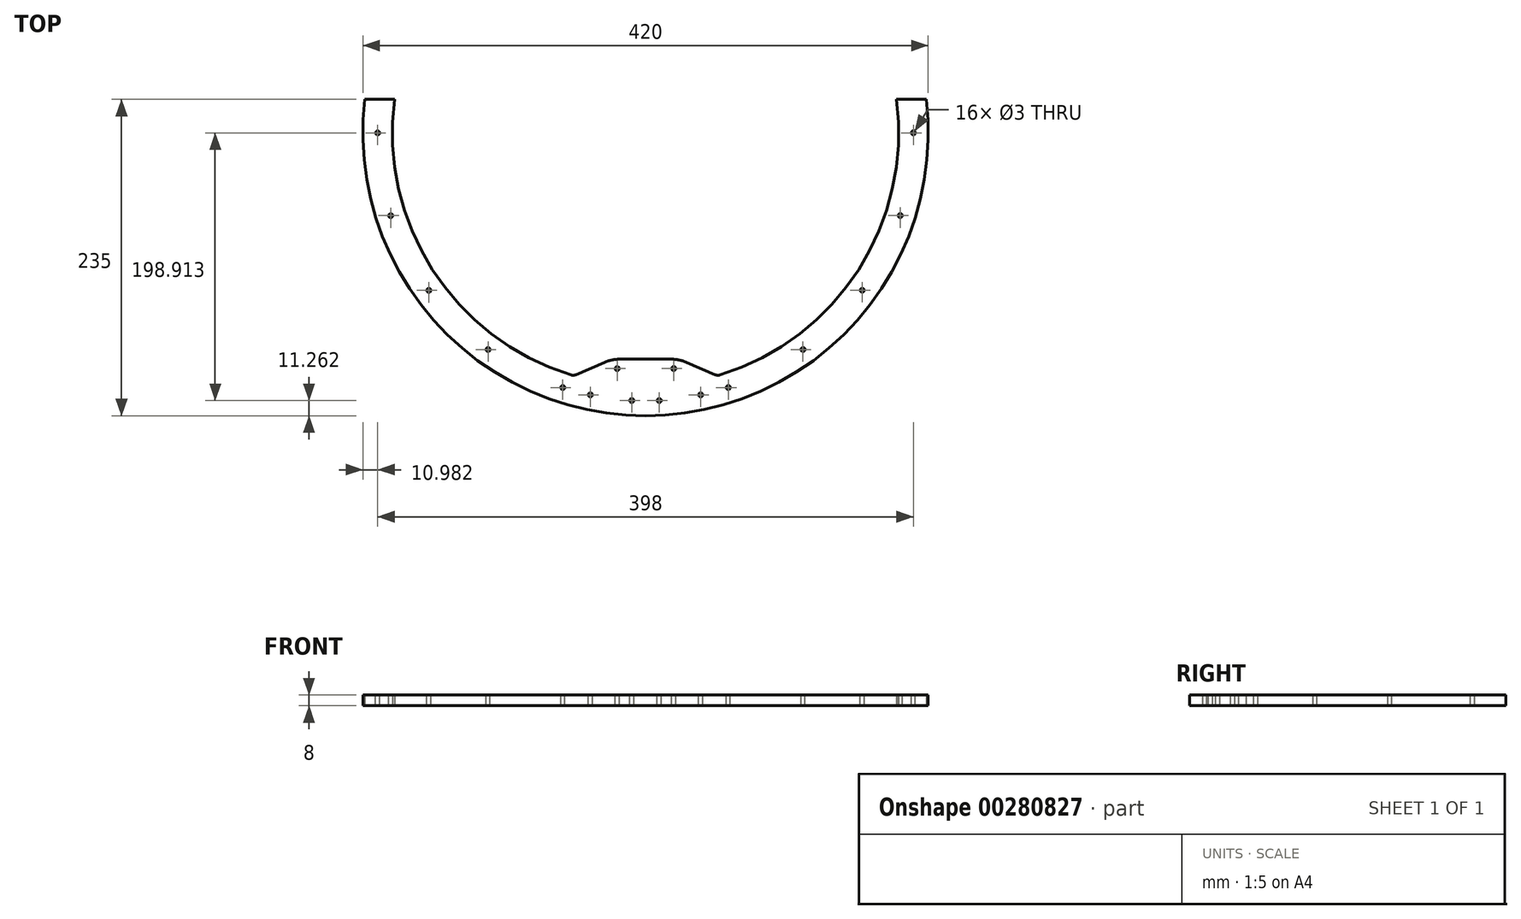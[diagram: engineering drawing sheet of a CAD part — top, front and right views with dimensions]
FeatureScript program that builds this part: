
annotation { "Feature Type Name" : "Feature", "Feature Type Description" : "" }
export const myFeature = defineFeature(function(context is Context, id is Id, definition is map)
    precondition{}
    {
        {
            var Q0;
            Q0=qCreatedBy(makeId("Top.planeOp"),FACE);
            var sketch = newSketch(context, id + "F0", { "sketchPlane" : qUnion([Q0])});
            skArc(sketch, "E0", {"start": v(-186.33, 25) * mm, "mid": v(-157.8, -102.18) * mm, "end": v(-53.43, -180.25) * mm});
            skArc(sketch, "E1", {"start": v(-208.5, 25) * mm, "mid": v(0, -210) * mm, "end": v(208.5, 25) * mm});
            skLineSegment(sketch, "E2", {"start": v(0, 0) * mm, "end": v(-114.72, 0) * mm, "construction": true});
            skLineSegment(sketch, "E3", {"start": v(0, 0) * mm, "end": v(0, 25) * mm, "construction": true});
            skLineSegment(sketch, "E4", {"start": v(186.33, 25) * mm, "end": v(208.5, 25) * mm});
            skLineSegment(sketch, "E5.MirrorCS", {"start": v(-186.33, 25) * mm, "end": v(-208.5, 25) * mm});
            skLineSegment(sketch, "E6", {"start": v(0, -188) * mm, "end": v(0, -168) * mm, "construction": true});
            skLineSegment(sketch, "E7", {"start": v(0, -168) * mm, "end": v(25, -168) * mm});
            skLineSegment(sketch, "E8", {"start": v(25, -168) * mm, "end": v(53.43, -180.25) * mm});
            skLineSegment(sketch, "E9.MirrorCS", {"start": v(0, -168) * mm, "end": v(-25, -168) * mm});
            skLineSegment(sketch, "E10.MirrorCS", {"start": v(-25, -168) * mm, "end": v(-53.43, -180.25) * mm});
            skArc(sketch, "E11.trimOffspring", {"start": v(53.43, -180.25) * mm, "mid": v(157.8, -102.18) * mm, "end": v(186.33, 25) * mm});
            skPoint(sketch, "E12.orphan", {"position": v(0, 25) * mm});
            skSolve(sketch);
        }
        {
            var Q0;
            Q0=qSketchRegion(id+"F0",true);
            extrude(context, id + "F1", {"entities" : qUnion([Q0]), "depth" : 8 * mm});
        }
        {
            var Q0;
            Q0=makeQuery(id+"F1.opExtrude","CAP_FACE",FACE,{"disambiguationData":[OSD([sQuery(id+"F0.wireOp",EDGE,"E0"),sQuery(id+"F0.wireOp",EDGE,"E1"),sQuery(id+"F0.wireOp",EDGE,"E4"),sQuery(id+"F0.wireOp",EDGE,"E5.MirrorCS"),sQuery(id+"F0.wireOp",EDGE,"E7"),sQuery(id+"F0.wireOp",EDGE,"E8"),sQuery(id+"F0.wireOp",EDGE,"E9.MirrorCS"),sQuery(id+"F0.wireOp",EDGE,"E10.MirrorCS"),sQuery(id+"F0.wireOp",EDGE,"E11.trimOffspring")])],"isStart":false});
            var sketch = newSketch(context, id + "F2", { "sketchPlane" : qUnion([Q0])});
            skArc(sketch, "E13.0", {"start": v(-198.1, 18.95) * mm, "mid": v(0, -199) * mm, "end": v(198.1, 18.95) * mm, "construction": true});
            skCircle(sketch, "E14.1.0", {"center": v(-61.5, -189.11) * mm, "radius": 1.5 * mm});
            skCircle(sketch, "E14.2.0", {"center": v(-116.97, -160.85) * mm, "radius": 1.5 * mm});
            skCircle(sketch, "E14.3.0", {"center": v(-161, -116.83) * mm, "radius": 1.5 * mm});
            skCircle(sketch, "E14.4.0", {"center": v(-189.27, -61.36) * mm, "radius": 1.5 * mm});
            skCircle(sketch, "E14.5.0", {"center": v(-199.02, 0.13) * mm, "radius": 1.5 * mm});
            skPoint(sketch, "E14.center", {"position": v(-0.02, 0.15) * mm});
            skLineSegment(sketch, "E14.anchor1", {"start": v(-0.02, 0.15) * mm, "end": v(0, -199) * mm, "construction": true});
            skLineSegment(sketch, "E14.anchor2", {"start": v(-0.02, 0.15) * mm, "end": v(-199.02, 0.13) * mm, "construction": true});
            skCircle(sketch, "E15.MirrorC", {"center": v(61.5, -189.1) * mm, "radius": 1.5 * mm});
            skCircle(sketch, "E16.MirrorC", {"center": v(116.97, -160.83) * mm, "radius": 1.5 * mm});
            skCircle(sketch, "E17.MirrorC", {"center": v(160.99, -116.8) * mm, "radius": 1.5 * mm});
            skCircle(sketch, "E18.MirrorC", {"center": v(189.25, -61.32) * mm, "radius": 1.5 * mm});
            skCircle(sketch, "E19.MirrorC", {"center": v(198.98, 0.18) * mm, "radius": 1.5 * mm});
            skLineSegment(sketch, "E20", {"start": v(0, -175) * mm, "end": v(-21, -175) * mm, "construction": true});
            skCircle(sketch, "E21", {"center": v(-21, -175) * mm, "radius": 1.5 * mm});
            skLineSegment(sketch, "E22", {"start": v(-21, -175) * mm, "end": v(-21, -195) * mm, "construction": true});
            skLineSegment(sketch, "E23", {"start": v(-21, -195) * mm, "end": v(-41, -194.45) * mm, "construction": true});
            skCircle(sketch, "E24", {"center": v(-41, -194.45) * mm, "radius": 1.5 * mm});
            skCircle(sketch, "E25", {"center": v(-10.2, -198.74) * mm, "radius": 1.5 * mm});
            skCircle(sketch, "E26.MirrorC", {"center": v(21, -175) * mm, "radius": 1.5 * mm});
            skCircle(sketch, "E27.MirrorC", {"center": v(10.2, -198.74) * mm, "radius": 1.5 * mm});
            skCircle(sketch, "E28.MirrorC", {"center": v(41, -194.44) * mm, "radius": 1.5 * mm});
            skSolve(sketch);
        }
        {
            var Q0;
            Q0=qSketchRegion(id+"F2",true);
            extrude(context, id + "F3", {"entities" : qUnion([Q0]), "operationType" : NewBodyOperationType.REMOVE, "endBound" : BoundingType.THROUGH_ALL, "oppositeDirection" : true, "depth" : 25 * mm});
        }
        {
            var Q0;
            Q0=makeQuery(id+"F1.opExtrude","SWEPT_EDGE",EDGE,{"disambiguationData":[OSD([sQuery(id+"F0.wireOp",EDGE,"E7"),sQuery(id+"F0.wireOp",EDGE,"E8")])]});
            var Q1;
            Q1=makeQuery(id+"F1.opExtrude","SWEPT_EDGE",EDGE,{"disambiguationData":[OSD([sQuery(id+"F0.wireOp",EDGE,"E9.MirrorCS"),sQuery(id+"F0.wireOp",EDGE,"E10.MirrorCS")])]});
            fillet(context, id + "F4", {"entities" : qUnion([Q0, Q1]), "radius" : 28.52 * mm, "tangentPropagation" : true, "allowEdgeOverflow" : false});
        }
        {
            var Q0;
            Q0=makeQuery(id+"F1.opExtrude","SWEPT_EDGE",EDGE,{"disambiguationData":[OSD([sQuery(id+"F0.wireOp",EDGE,"E8"),sQuery(id+"F0.wireOp",EDGE,"E11.trimOffspring")])]});
            var Q1;
            Q1=makeQuery(id+"F1.opExtrude","SWEPT_EDGE",EDGE,{"disambiguationData":[OSD([sQuery(id+"F0.wireOp",EDGE,"E0"),sQuery(id+"F0.wireOp",EDGE,"E10.MirrorCS")])]});
            fillet(context, id + "F5", {"entities" : qUnion([Q0, Q1]), "radius" : 5 * mm, "tangentPropagation" : true, "allowEdgeOverflow" : false});
        }
        {
            var Q0;
            Q0=qCreatedBy(makeId("Top.planeOp"),FACE);
            var sketch = newSketch(context, id + "F6", { "sketchPlane" : qUnion([Q0])});
            skLineSegment(sketch, "E29", {"start": v(0, 0) * mm, "end": v(174.2, -171.38) * mm, "construction": true});
            skLineSegment(sketch, "E30", {"start": v(0, 0) * mm, "end": v(0, 36.6) * mm, "construction": true});
            skLineSegment(sketch, "E31.MirrorCS", {"start": v(0, 0) * mm, "end": v(-174.2, -171.38) * mm, "construction": true});
            skSolve(sketch);
        }
    });
